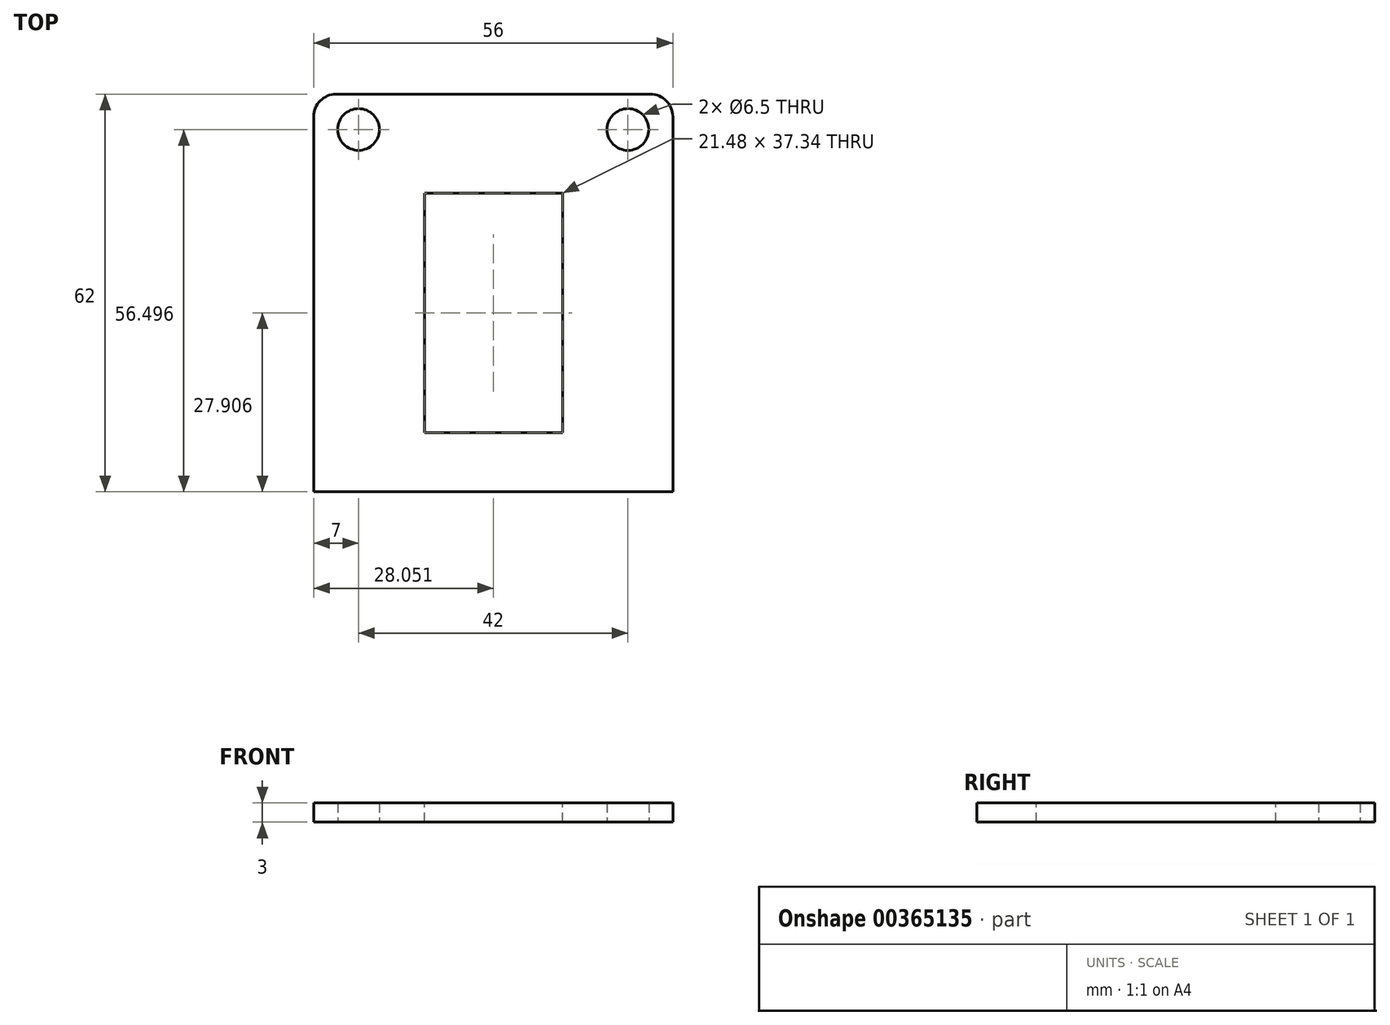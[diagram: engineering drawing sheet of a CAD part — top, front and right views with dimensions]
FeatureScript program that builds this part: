
annotation { "Feature Type Name" : "Feature", "Feature Type Description" : "" }
export const myFeature = defineFeature(function(context is Context, id is Id, definition is map)
    precondition{}
    {
        {
            var Q0;
            Q0=qCreatedBy(makeId("Top.planeOp"),FACE);
            var sketch = newSketch(context, id + "F0", { "sketchPlane" : qUnion([Q0])});
            skLineSegment(sketch, "E0.bottom", {"start": v(3.63, 48.36) * mm, "end": v(59.63, 48.36) * mm});
            skLineSegment(sketch, "E0.top", {"start": v(3.63, -13.64) * mm, "end": v(59.63, -13.64) * mm});
            skLineSegment(sketch, "E0.left", {"start": v(3.63, 48.36) * mm, "end": v(3.63, -13.64) * mm});
            skLineSegment(sketch, "E0.right", {"start": v(59.63, 48.36) * mm, "end": v(59.63, -13.64) * mm});
            skSolve(sketch);
        }
        {
            var Q0;
            Q0 = qSketchRegion(id + "F0", true);
            extrude(context, id + "F1", {"entities" : qUnion([Q0]), "depth" : 3 * mm});
        }
        {
            var Q0;
            Q0=qCreatedBy(makeId("Top.planeOp"),FACE);
            var sketch = newSketch(context, id + "F2", { "sketchPlane" : qUnion([Q0])});
            skCircle(sketch, "E1", {"center": v(52.63, 42.86) * mm, "radius": 3.25 * mm});
            skCircle(sketch, "E2", {"center": v(10.63, 42.86) * mm, "radius": 3.25 * mm});
            skSolve(sketch);
        }
        {
            var Q0;
            Q0 = qSketchRegion(id + "F2", true);
            extrude(context, id + "F3", {"entities" : qUnion([Q0]), "operationType" : NewBodyOperationType.REMOVE, "depth" : 3.5 * mm});
        }
        {
            var Q0;
            Q0=makeQuery(id+"F1.opExtrude","SWEPT_EDGE",EDGE,{"disambiguationData":[OSD([sQuery(id+"F0.wireOp",EDGE,"E0.bottom"),sQuery(id+"F0.wireOp",EDGE,"E0.left")])]});
            var Q1;
            Q1=makeQuery(id+"F1.opExtrude","SWEPT_EDGE",EDGE,{"disambiguationData":[OSD([sQuery(id+"F0.wireOp",EDGE,"E0.bottom"),sQuery(id+"F0.wireOp",EDGE,"E0.right")])]});
            fillet(context, id + "F4", {"entities" : qUnion([Q0, Q1]), "radius" : 3.5 * mm, "tangentPropagation" : true, "allowEdgeOverflow" : false});
        }
        {
            var Q0;
            Q0=makeQuery(id+"F1.opExtrude","CAP_FACE",FACE,{"disambiguationData":[OSD([sQuery(id+"F0.wireOp",EDGE,"E0.bottom"),sQuery(id+"F0.wireOp",EDGE,"E0.top"),sQuery(id+"F0.wireOp",EDGE,"E0.left"),sQuery(id+"F0.wireOp",EDGE,"E0.right")])],"isStart":false});
            var sketch = newSketch(context, id + "F5", { "sketchPlane" : qUnion([Q0])});
            skLineSegment(sketch, "E3.bottom", {"start": v(20.94, 32.94) * mm, "end": v(42.42, 32.94) * mm});
            skLineSegment(sketch, "E3.top", {"start": v(20.94, -4.4) * mm, "end": v(42.42, -4.4) * mm});
            skLineSegment(sketch, "E3.left", {"start": v(20.94, 32.94) * mm, "end": v(20.94, -4.4) * mm});
            skLineSegment(sketch, "E3.right", {"start": v(42.42, 32.94) * mm, "end": v(42.42, -4.4) * mm});
            skSolve(sketch);
        }
        {
            var Q0;
            Q0 = qSketchRegion(id + "F5", true);
            extrude(context, id + "F6", {"entities" : qUnion([Q0]), "operationType" : NewBodyOperationType.REMOVE, "oppositeDirection" : true, "depth" : 3.5 * mm});
        }
    });
